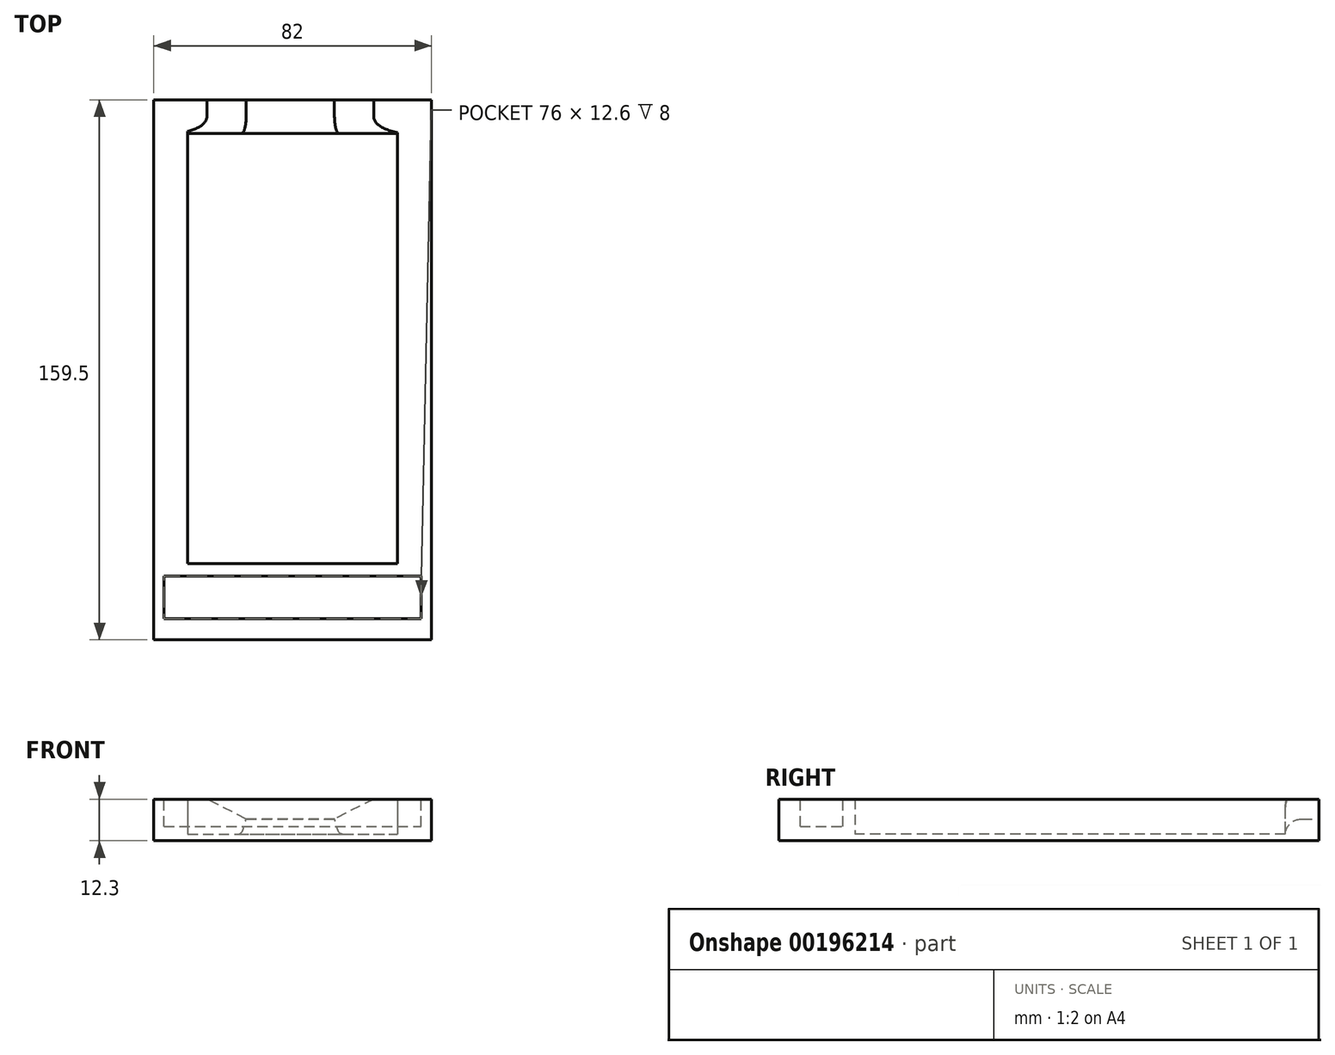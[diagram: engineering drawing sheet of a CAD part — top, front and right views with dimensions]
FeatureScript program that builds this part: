
annotation { "Feature Type Name" : "Feature", "Feature Type Description" : "" }
export const myFeature = defineFeature(function(context is Context, id is Id, definition is map)
    precondition{}
    {
        {
            var Q0;
            Q0=qCreatedBy(makeId("Top.planeOp"),FACE);
            var sketch = newSketch(context, id + "F0", { "sketchPlane" : qUnion([Q0])});
            skLineSegment(sketch, "E0.bottom", {"start": v(-30.1, 51.55) * mm, "end": v(31.9, 51.55) * mm});
            skLineSegment(sketch, "E0.top", {"start": v(-30.1, -75.45) * mm, "end": v(31.9, -75.45) * mm});
            skLineSegment(sketch, "E0.left", {"start": v(-30.1, 51.55) * mm, "end": v(-30.1, -75.45) * mm});
            skLineSegment(sketch, "E0.right", {"start": v(31.9, 51.55) * mm, "end": v(31.9, -75.45) * mm});
            skLineSegment(sketch, "E1.0", {"start": v(-40.1, 61.55) * mm, "end": v(-40.1, -85.45) * mm});
            skLineSegment(sketch, "E1.1", {"start": v(-40.1, 61.55) * mm, "end": v(41.9, 61.55) * mm});
            skLineSegment(sketch, "E1.2", {"start": v(41.9, 61.55) * mm, "end": v(41.9, -85.45) * mm});
            skLineSegment(sketch, "E1.3", {"start": v(-40.1, -85.45) * mm, "end": v(41.9, -85.45) * mm});
            skSolve(sketch);
        }
        {
            var Q0;
            Q0=makeQuery(id+"F0.imprint","IMPRINT",FACE,{"disambiguationData":[TD([[makeQuery(id+"F0.imprint","IMPRINT",EDGE,{"derivedFrom":sQuery(id+"F0.wireOp",EDGE,"E0.bottom")}),1.0]])]});
            extrude(context, id + "F1", {"entities" : qUnion([Q0]), "depth" : 12.3 * mm});
        }
        {
            var Q0;
            Q0=makeQuery(id+"F0.imprint","IMPRINT",FACE,{"disambiguationData":[TD([[makeQuery(id+"F0.imprint","IMPRINT",EDGE,{"derivedFrom":sQuery(id+"F0.wireOp",EDGE,"E0.bottom")}),-1.0]])]});
            extrude(context, id + "F2", {"entities" : qUnion([Q0]), "operationType" : NewBodyOperationType.ADD, "depth" : 2 * mm});
        }
        {
            var Q0;
            Q0=makeQuery(id+"F1.opExtrude","SWEPT_FACE",FACE,{"disambiguationData":[OSD([sQuery(id+"F0.wireOp",EDGE,"E1.1")])]});
            var sketch = newSketch(context, id + "F3", { "sketchPlane" : qUnion([Q0])});
            skLineSegment(sketch, "E2", {"start": v(-24.85, 12.3) * mm, "end": v(-13.25, 6.44) * mm});
            skLineSegment(sketch, "E3", {"start": v(-13.25, 6.44) * mm, "end": v(12.82, 6.44) * mm});
            skLineSegment(sketch, "E4", {"start": v(12.82, 6.44) * mm, "end": v(24.42, 12.3) * mm});
            skLineSegment(sketch, "E5", {"start": v(24.42, 12.3) * mm, "end": v(-24.85, 12.3) * mm});
            skSolve(sketch);
        }
        {
            var Q0;
            Q0=makeQuery(id+"F1.opExtrude","SWEPT_FACE",FACE,{"disambiguationData":[OSD([sQuery(id+"F0.wireOp",EDGE,"E1.3")])]});
            extrude(context, id + "F4", {"entities" : qUnion([Q0]), "operationType" : NewBodyOperationType.ADD, "depth" : 12.5 * mm});
        }
        {
            var Q0;
            {var subQ0=sQuery(id+"F0.wireOp",EDGE,"E1.3");Q0=makeQuery(id+"F4.boolean.opBoolean","MERGE",FACE,{"derivedFrom":[makeQuery(id+"F1.opExtrude","CAP_FACE",FACE,{"disambiguationData":[OSD([sQuery(id+"F0.wireOp",EDGE,"E0.bottom"),sQuery(id+"F0.wireOp",EDGE,"E0.top"),sQuery(id+"F0.wireOp",EDGE,"E0.left"),sQuery(id+"F0.wireOp",EDGE,"E0.right"),sQuery(id+"F0.wireOp",EDGE,"E1.0"),sQuery(id+"F0.wireOp",EDGE,"E1.1"),sQuery(id+"F0.wireOp",EDGE,"E1.2"),subQ0])],"isStart":false}),makeQuery(id+"F4.opExtrude","SWEPT_FACE",FACE,{"disambiguationData":[OSD([subQ0]),TDD([makeQuery(id+"F1.opExtrude","CAP_EDGE",EDGE,{"disambiguationData":[OSD([subQ0])],"isStart":false})])]})]});}
            var sketch = newSketch(context, id + "F5", { "sketchPlane" : qUnion([Q0])});
            skLineSegment(sketch, "E6.bottom", {"start": v(-37.1, -91.66) * mm, "end": v(38.9, -91.66) * mm});
            skLineSegment(sketch, "E6.top", {"start": v(-37.1, -79.06) * mm, "end": v(38.9, -79.06) * mm});
            skLineSegment(sketch, "E6.left", {"start": v(-37.1, -91.66) * mm, "end": v(-37.1, -79.06) * mm});
            skLineSegment(sketch, "E6.right", {"start": v(38.9, -91.66) * mm, "end": v(38.9, -79.06) * mm});
            skPoint(sketch, "E6.middle", {"position": v(0.9, -85.36) * mm});
            skSolve(sketch);
        }
        {
            var Q0;
            Q0 = qSketchRegion(id + "F5", true);
            extrude(context, id + "F6", {"entities" : qUnion([Q0]), "operationType" : NewBodyOperationType.REMOVE, "oppositeDirection" : true, "depth" : 8 * mm});
        }
        {
            var Q0;
            Q0=makeQuery(id+"F3.imprint","IMPRINT",FACE,{"disambiguationData":[TD([[makeQuery(id+"F3.imprint","IMPRINT",EDGE,{"derivedFrom":sQuery(id+"F3.wireOp",EDGE,"E2")}),1.0]])]});
            extrude(context, id + "F7", {"entities" : qUnion([Q0]), "operationType" : NewBodyOperationType.REMOVE, "oppositeDirection" : true, "depth" : 25 * mm});
        }
        {
            var Q0;
            Q0=makeQuery(id+"F7.boolean.opBoolean","INTERSECT",EDGE,{"derivedFrom":[makeQuery(id+"F1.opExtrude","SWEPT_FACE",FACE,{"disambiguationData":[OSD([sQuery(id+"F0.wireOp",EDGE,"E0.bottom")])]}),makeQuery(id+"F7.opExtrude","SWEPT_FACE",FACE,{"disambiguationData":[OSD([sQuery(id+"F3.wireOp",EDGE,"E4")])]})]});
            var Q1;
            Q1=makeQuery(id+"F7.boolean.opBoolean","INTERSECT",EDGE,{"derivedFrom":[makeQuery(id+"F1.opExtrude","SWEPT_FACE",FACE,{"disambiguationData":[OSD([sQuery(id+"F0.wireOp",EDGE,"E0.bottom")])]}),makeQuery(id+"F7.opExtrude","SWEPT_FACE",FACE,{"disambiguationData":[OSD([sQuery(id+"F3.wireOp",EDGE,"E3")])]})]});
            var Q2;
            Q2=makeQuery(id+"F7.boolean.opBoolean","INTERSECT",EDGE,{"derivedFrom":[makeQuery(id+"F1.opExtrude","SWEPT_FACE",FACE,{"disambiguationData":[OSD([sQuery(id+"F0.wireOp",EDGE,"E0.bottom")])]}),makeQuery(id+"F7.opExtrude","SWEPT_FACE",FACE,{"disambiguationData":[OSD([sQuery(id+"F3.wireOp",EDGE,"E2")])]})]});
            fillet(context, id + "F8", {"entities" : qUnion([Q0, Q1, Q2]), "radius" : 5 * mm, "tangentPropagation" : true, "allowEdgeOverflow" : false});
        }
    });
